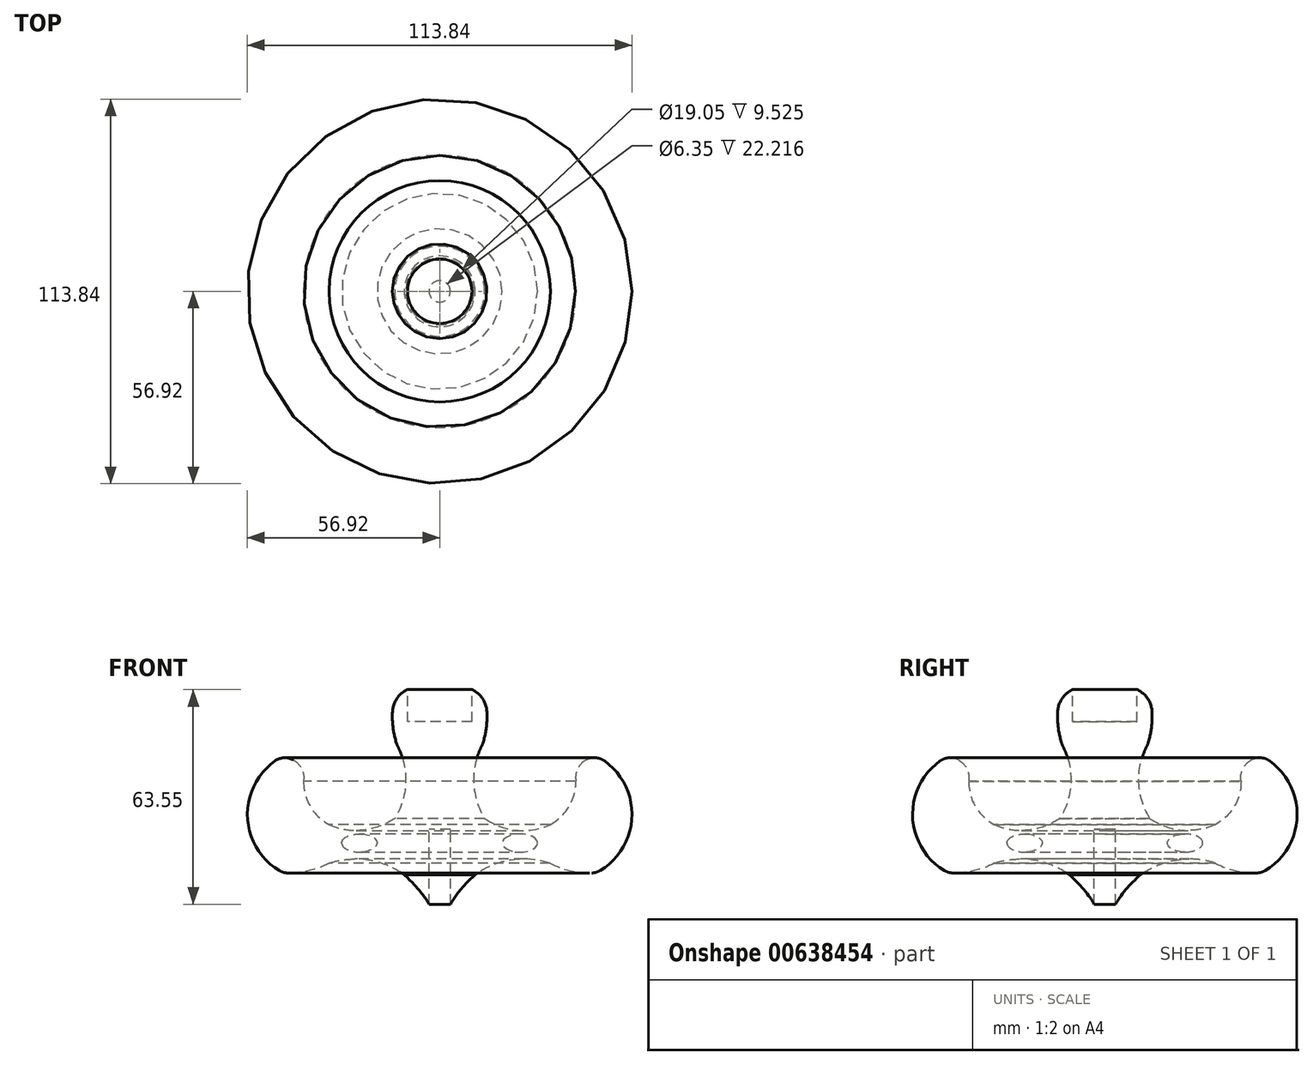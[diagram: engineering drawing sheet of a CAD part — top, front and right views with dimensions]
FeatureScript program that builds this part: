
annotation { "Feature Type Name" : "Feature", "Feature Type Description" : "" }
export const myFeature = defineFeature(function(context is Context, id is Id, definition is map)
    precondition{}
    {
        {
            var Q0;
            Q0=qCreatedBy(makeId("Front.planeOp"),FACE);
            var sketch = newSketch(context, id + "F0", { "sketchPlane" : qUnion([Q0])});
            skPoint(sketch, "E0.start.orphan", {"position": v(53.97, 11.23) * mm});
            skArc(sketch, "E1", {"start": v(32.72, 12.18) * mm, "mid": v(21.19, 13.1) * mm, "end": v(10.48, 8.7) * mm});
            skFitSpline(sketch, "E2", {"points": [v(3.18, 0) * mm, v(10.48, 8.7) * mm], "startDerivative": vector(4.82, 8.95) * mm, "endDerivative": vector(9.76, 8.9) * mm});
            skArc(sketch, "E3", {"start": v(32.72, 12.18) * mm, "mid": v(39.31, 9.77) * mm, "end": v(46.32, 9.33) * mm});
            skLineSegment(sketch, "E4", {"start": v(0, 54.04) * mm, "end": v(0, 22.23) * mm});
            skLineSegment(sketch, "E5", {"start": v(9.53, 63.56) * mm, "end": v(9.53, 54.04) * mm});
            skLineSegment(sketch, "E6", {"start": v(9.53, 54.04) * mm, "end": v(0, 54.04) * mm});
            skPoint(sketch, "E7.end.orphan", {"position": v(3.17, 0) * mm});
            skLineSegment(sketch, "E8", {"start": v(3.18, 0) * mm, "end": v(3.18, 22.23) * mm});
            skLineSegment(sketch, "E9", {"start": v(0, 22.23) * mm, "end": v(3.18, 22.23) * mm});
            skArc(sketch, "E10", {"start": v(12.63, 47.17) * mm, "mid": v(10.06, 36.2) * mm, "end": v(13.31, 25.42) * mm});
            skArc(sketch, "E11", {"start": v(13.31, 25.42) * mm, "mid": v(22.8, 21.94) * mm, "end": v(32.77, 23.59) * mm});
            skArc(sketch, "E12", {"start": v(32.77, 23.59) * mm, "mid": v(38.3, 28.97) * mm, "end": v(40.33, 36.4) * mm});
            skLineSegment(sketch, "E13", {"start": v(9.53, 63.56) * mm, "end": v(12.8, 63.6) * mm});
            skArc(sketch, "E14", {"start": v(46.32, 9.33) * mm, "mid": v(56.91, 26.14) * mm, "end": v(47.2, 43.46) * mm});
            skArc(sketch, "E15", {"start": v(47.2, 43.46) * mm, "mid": v(41.96, 41.68) * mm, "end": v(40.33, 36.4) * mm});
            skArc(sketch, "E16", {"start": v(12.8, 63.6) * mm, "mid": v(12.8, 63.63) * mm, "end": v(12.8, 63.65) * mm});
            skPoint(sketch, "E16.endSnap0", {"position": v(12.8, 63.6) * mm});
            skArc(sketch, "E17", {"start": v(12.63, 47.17) * mm, "mid": v(14, 55.37) * mm, "end": v(12.8, 63.6) * mm});
            skPoint(sketch, "E18", {"position": v(23.76, 13.36) * mm});
            skEllipse(sketch, "E19", {"center": v(23.76, 18.14) * mm, "majorRadius": 5.22 * mm, "minorRadius": 2.7 * mm, "majorAxis": v(1, 0)});
            skSolve(sketch);
        }
        {
            var Q0;
            Q0=makeQuery(id+"F0.imprint","IMPRINT",FACE,{"disambiguationData":[TD([[makeQuery(id+"F0.imprint","IMPRINT",EDGE,{"derivedFrom":sQuery(id+"F0.wireOp",EDGE,"E1")}),-1.0]])]});
            var Q1;
            Q1=sQuery(id+"F0.wireOp",EDGE,"E4");
            revolve(context, id + "F1", {"entities" : qUnion([Q0]), "axis" : qUnion([Q1]), "revolveType" : RevolveType.FULL});
        }
        {
            var Q0;
            Q0=makeQuery(id+"F1.opRevolve","SWEPT_FACE",FACE,{"disambiguationData":[OSD([sQuery(id+"F0.wireOp",EDGE,"E17")])]});
            fillet(context, id + "F2", {"entities" : qUnion([Q0]), "radius" : 7.62 * mm, "tangentPropagation" : true, "allowEdgeOverflow" : false});
        }
        {
            var Q0;
            Q0=makeQuery(id+"F1.opRevolve","SWEPT_EDGE",EDGE,{"disambiguationData":[OSD([sQuery(id+"F0.wireOp",EDGE,"E14"),sQuery(id+"F0.wireOp",EDGE,"E15")])]});
            var Q1;
            Q1=makeQuery(id+"F1.opRevolve","SWEPT_FACE",FACE,{"disambiguationData":[OSD([sQuery(id+"F0.wireOp",EDGE,"E14")])]});
            fillet(context, id + "F3", {"entities" : qUnion([Q0, Q1]), "radius" : 5.08 * mm, "tangentPropagation" : true, "allowEdgeOverflow" : false});
        }
    });
